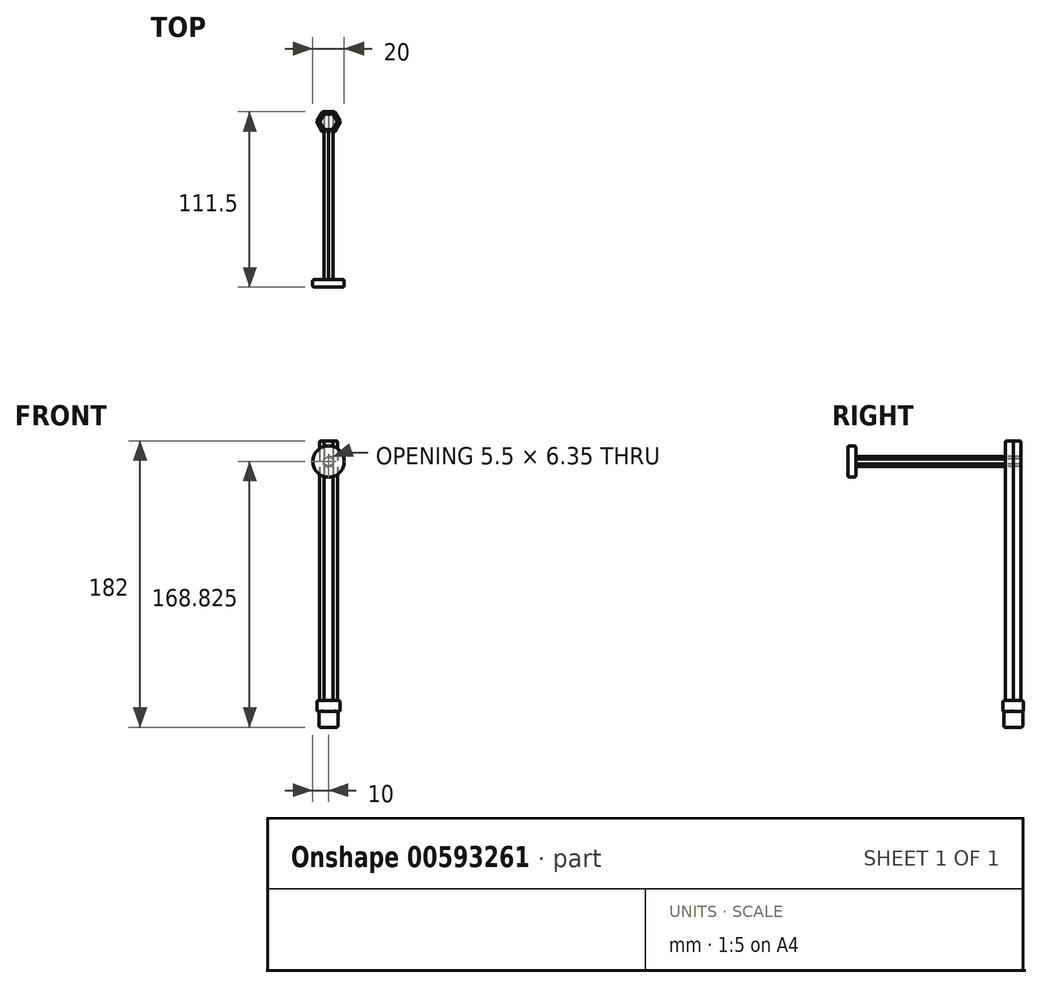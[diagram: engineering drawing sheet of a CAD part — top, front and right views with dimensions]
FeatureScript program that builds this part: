
annotation { "Feature Type Name" : "Feature", "Feature Type Description" : "" }
export const myFeature = defineFeature(function(context is Context, id is Id, definition is map)
    precondition{}
    {
        {
            var Q0;
            Q0=qCreatedBy(makeId("Top.planeOp"),FACE);
            var sketch = newSketch(context, id + "F0", { "sketchPlane" : qUnion([Q0])});
            skCircle(sketch, "E0", {"center": v(0, 0) * mm, "radius": 6 * mm});
            skSolve(sketch);
        }
        {
            var Q0;
            Q0=makeQuery(id+"F0.imprint","IMPRINT",FACE,{"disambiguationData":[TD([[makeQuery(id+"F0.imprint","IMPRINT",EDGE,{"derivedFrom":sQuery(id+"F0.wireOp",EDGE,"E0")}),1.0]])]});
            extrude(context, id + "F1", {"entities" : qUnion([Q0]), "depth" : 17 * mm, "offsetDistance" : 25 * mm});
        }
        {
            var Q0;
            Q0=makeQuery(id+"F1.opExtrude","CAP_FACE",FACE,{"disambiguationData":[OSD([sQuery(id+"F0.wireOp",EDGE,"E0")])],"isStart":false});
            var sketch = newSketch(context, id + "F2", { "sketchPlane" : qUnion([Q0])});
            skCircle(sketch, "E1.cCircle", {"center": v(0, 0) * mm, "radius": 5.47 * mm, "construction": true});
            skCircle(sketch, "E2.cCircle", {"center": v(0, 0) * mm, "radius": 6.5 * mm, "construction": true});
            skLineSegment(sketch, "E2.0", {"start": v(3.75, 6.5) * mm, "end": v(7.5, 0) * mm});
            skLineSegment(sketch, "E2.1", {"start": v(7.5, 0) * mm, "end": v(3.75, -6.5) * mm});
            skLineSegment(sketch, "E2.2", {"start": v(3.75, -6.5) * mm, "end": v(-3.75, -6.5) * mm});
            skLineSegment(sketch, "E2.3", {"start": v(-3.75, -6.5) * mm, "end": v(-7.5, 0) * mm});
            skLineSegment(sketch, "E2.4", {"start": v(-7.5, 0) * mm, "end": v(-3.75, 6.5) * mm});
            skLineSegment(sketch, "E2.5", {"start": v(-3.75, 6.5) * mm, "end": v(3.75, 6.5) * mm});
            skPoint(sketch, "E2.0.midPoint", {"position": v(5.63, 3.25) * mm});
            skSolve(sketch);
        }
        {
            var Q0;
            Q0=makeQuery(id+"F2.imprint","IMPRINT",FACE,{"disambiguationData":[TD([[makeQuery(id+"F2.imprint","IMPRINT",EDGE,{"derivedFrom":sQuery(id+"F2.wireOp",EDGE,"E2.0")}),-1.0]])]});
            extrude(context, id + "F3", {"entities" : qUnion([Q0]), "operationType" : NewBodyOperationType.ADD, "oppositeDirection" : true, "depth" : 7 * mm, "offsetDistance" : 25 * mm});
        }
        {
            var Q0;
            {var subQ0=sQuery(id+"F0.wireOp",EDGE,"E0");Q0=makeQuery(id+"F3.boolean.opBoolean","MERGE",FACE,{"derivedFrom":[makeQuery(id+"F1.opExtrude","CAP_FACE",FACE,{"disambiguationData":[OSD([subQ0])],"isStart":false}),makeQuery(id+"F3.opExtrude","CAP_FACE",FACE,{"disambiguationData":[OSD([subQ0,sQuery(id+"F2.wireOp",EDGE,"E2.0"),sQuery(id+"F2.wireOp",EDGE,"E2.1"),sQuery(id+"F2.wireOp",EDGE,"E2.2"),sQuery(id+"F2.wireOp",EDGE,"E2.3"),sQuery(id+"F2.wireOp",EDGE,"E2.4"),sQuery(id+"F2.wireOp",EDGE,"E2.5")])],"isStart":true})]});}
            var sketch = newSketch(context, id + "F4", { "sketchPlane" : qUnion([Q0])});
            skCircle(sketch, "E3.cCircle", {"center": v(0, 0) * mm, "radius": 5 * mm, "construction": true});
            skLineSegment(sketch, "E3.0", {"start": v(5.77, 0) * mm, "end": v(2.89, -5) * mm});
            skLineSegment(sketch, "E3.1", {"start": v(2.89, -5) * mm, "end": v(-2.89, -5) * mm});
            skLineSegment(sketch, "E3.2", {"start": v(-2.89, -5) * mm, "end": v(-5.77, 0) * mm});
            skLineSegment(sketch, "E3.3", {"start": v(-5.77, 0) * mm, "end": v(-2.89, 5) * mm});
            skLineSegment(sketch, "E3.4", {"start": v(-2.89, 5) * mm, "end": v(2.89, 5) * mm});
            skLineSegment(sketch, "E3.5", {"start": v(2.89, 5) * mm, "end": v(5.77, 0) * mm});
            skPoint(sketch, "E3.0.midPoint", {"position": v(4.33, -2.5) * mm});
            skSolve(sketch);
        }
        {
            var Q0;
            Q0=makeQuery(id+"F4.imprint","IMPRINT",FACE,{"disambiguationData":[TD([[makeQuery(id+"F4.imprint","IMPRINT",EDGE,{"derivedFrom":sQuery(id+"F4.wireOp",EDGE,"E3.0")}),-1.0]])]});
            extrude(context, id + "F5", {"entities" : qUnion([Q0]), "operationType" : NewBodyOperationType.REMOVE, "oppositeDirection" : true, "depth" : 15 * mm, "offsetDistance" : 25 * mm});
        }
        {
            var Q0;
            Q0=makeQuery(id+"F3.opExtrude","SWEPT_FACE",FACE,{"disambiguationData":[OSD([sQuery(id+"F2.wireOp",EDGE,"E2.0")])]});
            var Q1;
            Q1=makeQuery(id+"F3.opExtrude","SWEPT_FACE",FACE,{"disambiguationData":[OSD([sQuery(id+"F2.wireOp",EDGE,"E2.5")])]});
            var Q2;
            Q2=makeQuery(id+"F3.opExtrude","SWEPT_FACE",FACE,{"disambiguationData":[OSD([sQuery(id+"F2.wireOp",EDGE,"E2.4")])]});
            var Q3;
            Q3=makeQuery(id+"F3.opExtrude","SWEPT_FACE",FACE,{"disambiguationData":[OSD([sQuery(id+"F2.wireOp",EDGE,"E2.3")])]});
            var Q4;
            Q4=makeQuery(id+"F3.opExtrude","SWEPT_FACE",FACE,{"disambiguationData":[OSD([sQuery(id+"F2.wireOp",EDGE,"E2.2")])]});
            var Q5;
            Q5=makeQuery(id+"F3.opExtrude","SWEPT_FACE",FACE,{"disambiguationData":[OSD([sQuery(id+"F2.wireOp",EDGE,"E2.1")])]});
            var Q6;
            Q6=makeQuery(id+"F1.opExtrude","CAP_EDGE",EDGE,{"disambiguationData":[OSD([sQuery(id+"F0.wireOp",EDGE,"E0")])],"isStart":true});
            fillet(context, id + "F6", {"entities" : qUnion([Q0, Q1, Q2, Q3, Q4, Q5, Q6]), "radius" : 1 * mm, "tangentPropagation" : true, "allowEdgeOverflow" : false});
        }
        {
            var Q0;
            Q0=makeQuery(id+"F5.boolean.opBoolean","COPY",FACE,{"derivedFrom":makeQuery(id+"F5.opExtrude","CAP_FACE",FACE,{"disambiguationData":[OSD([sQuery(id+"F4.wireOp",EDGE,"E3.0"),sQuery(id+"F4.wireOp",EDGE,"E3.1"),sQuery(id+"F4.wireOp",EDGE,"E3.2"),sQuery(id+"F4.wireOp",EDGE,"E3.3"),sQuery(id+"F4.wireOp",EDGE,"E3.4"),sQuery(id+"F4.wireOp",EDGE,"E3.5")])],"isStart":false})});
            extrude(context, id + "F7", {"entities" : qUnion([Q0]), "operationType" : NewBodyOperationType.ADD, "depth" : 180 * mm, "offsetDistance" : 25 * mm});
        }
        {
            var Q0;
            Q0=makeQuery(id+"F7.opExtrude","SWEPT_FACE",FACE,{"disambiguationData":[OSD([sQuery(id+"F4.wireOp",EDGE,"E3.1")])]});
            var sketch = newSketch(context, id + "F8", { "sketchPlane" : qUnion([Q0])});
            skCircle(sketch, "E4.cCircle", {"center": v(0, 168.82) * mm, "radius": 2.75 * mm, "construction": true});
            skPoint(sketch, "E4.cCircle.centerSnap0", {"position": v(0, 182) * mm});
            skLineSegment(sketch, "E4.0", {"start": v(0, 172) * mm, "end": v(2.75, 170.41) * mm});
            skLineSegment(sketch, "E4.1", {"start": v(2.75, 170.41) * mm, "end": v(2.75, 167.24) * mm});
            skLineSegment(sketch, "E4.2", {"start": v(2.75, 167.24) * mm, "end": v(0, 165.65) * mm});
            skLineSegment(sketch, "E4.3", {"start": v(0, 165.65) * mm, "end": v(-2.75, 167.24) * mm});
            skLineSegment(sketch, "E4.4", {"start": v(-2.75, 167.24) * mm, "end": v(-2.75, 170.41) * mm});
            skLineSegment(sketch, "E4.5", {"start": v(-2.75, 170.41) * mm, "end": v(0, 172) * mm});
            skPoint(sketch, "E4.0.midPoint", {"position": v(1.38, 171.2) * mm});
            skSolve(sketch);
        }
        {
            var Q0;
            Q0=makeQuery(id+"F8.imprint","IMPRINT",FACE,{"disambiguationData":[TD([[makeQuery(id+"F8.imprint","IMPRINT",EDGE,{"derivedFrom":sQuery(id+"F8.wireOp",EDGE,"E4.0")}),-1.0]])]});
            extrude(context, id + "F9", {"entities" : qUnion([Q0]), "operationType" : NewBodyOperationType.REMOVE, "endBound" : BoundingType.THROUGH_ALL, "oppositeDirection" : true, "depth" : 25 * mm, "offsetDistance" : 25 * mm});
        }
        {
            var Q0;
            Q0=makeQuery(id+"F8.imprint","IMPRINT",FACE,{"disambiguationData":[TD([[makeQuery(id+"F8.imprint","IMPRINT",EDGE,{"derivedFrom":sQuery(id+"F8.wireOp",EDGE,"E4.0")}),-1.0]])]});
            extrude(context, id + "F10", {"entities" : qUnion([Q0]), "depth" : 100 * mm, "offsetDistance" : 25 * mm});
        }
        {
            var Q0;
            Q0=makeQuery(id+"F10.opExtrude","CAP_FACE",FACE,{"disambiguationData":[OSD([sQuery(id+"F8.wireOp",EDGE,"E4.0"),sQuery(id+"F8.wireOp",EDGE,"E4.1"),sQuery(id+"F8.wireOp",EDGE,"E4.2"),sQuery(id+"F8.wireOp",EDGE,"E4.3"),sQuery(id+"F8.wireOp",EDGE,"E4.4"),sQuery(id+"F8.wireOp",EDGE,"E4.5")])],"isStart":false});
            fillet(context, id + "F11", {"entities" : qUnion([Q0]), "radius" : 1 * mm, "tangentPropagation" : true, "allowEdgeOverflow" : false});
        }
        {
            var Q0;
            Q0=makeQuery(id+"F9.boolean.opBoolean","INTERSECT",EDGE,{"derivedFrom":[makeQuery(id+"F7.opExtrude","SWEPT_FACE",FACE,{"disambiguationData":[OSD([sQuery(id+"F4.wireOp",EDGE,"E3.4")])]}),makeQuery(id+"F9.opExtrude","SWEPT_FACE",FACE,{"disambiguationData":[OSD([sQuery(id+"F8.wireOp",EDGE,"E4.5")])]})]});
            var Q1;
            Q1=makeQuery(id+"F9.boolean.opBoolean","INTERSECT",EDGE,{"derivedFrom":[makeQuery(id+"F7.opExtrude","SWEPT_FACE",FACE,{"disambiguationData":[OSD([sQuery(id+"F4.wireOp",EDGE,"E3.4")])]}),makeQuery(id+"F9.opExtrude","SWEPT_FACE",FACE,{"disambiguationData":[OSD([sQuery(id+"F8.wireOp",EDGE,"E4.0")])]})]});
            var Q2;
            Q2=makeQuery(id+"F9.boolean.opBoolean","INTERSECT",EDGE,{"derivedFrom":[makeQuery(id+"F7.opExtrude","SWEPT_FACE",FACE,{"disambiguationData":[OSD([sQuery(id+"F4.wireOp",EDGE,"E3.4")])]}),makeQuery(id+"F9.opExtrude","SWEPT_FACE",FACE,{"disambiguationData":[OSD([sQuery(id+"F8.wireOp",EDGE,"E4.1")])]})]});
            var Q3;
            Q3=makeQuery(id+"F9.boolean.opBoolean","INTERSECT",EDGE,{"derivedFrom":[makeQuery(id+"F7.opExtrude","SWEPT_FACE",FACE,{"disambiguationData":[OSD([sQuery(id+"F4.wireOp",EDGE,"E3.4")])]}),makeQuery(id+"F9.opExtrude","SWEPT_FACE",FACE,{"disambiguationData":[OSD([sQuery(id+"F8.wireOp",EDGE,"E4.2")])]})]});
            var Q4;
            Q4=makeQuery(id+"F9.boolean.opBoolean","INTERSECT",EDGE,{"derivedFrom":[makeQuery(id+"F7.opExtrude","SWEPT_FACE",FACE,{"disambiguationData":[OSD([sQuery(id+"F4.wireOp",EDGE,"E3.4")])]}),makeQuery(id+"F9.opExtrude","SWEPT_FACE",FACE,{"disambiguationData":[OSD([sQuery(id+"F8.wireOp",EDGE,"E4.3")])]})]});
            var Q5;
            Q5=makeQuery(id+"F9.boolean.opBoolean","INTERSECT",EDGE,{"derivedFrom":[makeQuery(id+"F7.opExtrude","SWEPT_FACE",FACE,{"disambiguationData":[OSD([sQuery(id+"F4.wireOp",EDGE,"E3.4")])]}),makeQuery(id+"F9.opExtrude","SWEPT_FACE",FACE,{"disambiguationData":[OSD([sQuery(id+"F8.wireOp",EDGE,"E4.4")])]})]});
            var Q6;
            Q6=makeQuery(id+"F9.boolean.opBoolean","COPY",EDGE,{"derivedFrom":makeQuery(id+"F9.opExtrude","CAP_EDGE",EDGE,{"disambiguationData":[OSD([sQuery(id+"F8.wireOp",EDGE,"E4.0")])],"isStart":true})});
            var Q7;
            Q7=makeQuery(id+"F9.boolean.opBoolean","COPY",EDGE,{"derivedFrom":makeQuery(id+"F9.opExtrude","CAP_EDGE",EDGE,{"disambiguationData":[OSD([sQuery(id+"F8.wireOp",EDGE,"E4.5")])],"isStart":true})});
            var Q8;
            Q8=makeQuery(id+"F9.boolean.opBoolean","COPY",EDGE,{"derivedFrom":makeQuery(id+"F9.opExtrude","CAP_EDGE",EDGE,{"disambiguationData":[OSD([sQuery(id+"F8.wireOp",EDGE,"E4.3")])],"isStart":true})});
            var Q9;
            Q9=makeQuery(id+"F9.boolean.opBoolean","COPY",EDGE,{"derivedFrom":makeQuery(id+"F9.opExtrude","CAP_EDGE",EDGE,{"disambiguationData":[OSD([sQuery(id+"F8.wireOp",EDGE,"E4.2")])],"isStart":true})});
            var Q10;
            Q10=makeQuery(id+"F9.boolean.opBoolean","COPY",EDGE,{"derivedFrom":makeQuery(id+"F9.opExtrude","CAP_EDGE",EDGE,{"disambiguationData":[OSD([sQuery(id+"F8.wireOp",EDGE,"E4.1")])],"isStart":true})});
            var Q11;
            Q11=makeQuery(id+"F9.boolean.opBoolean","COPY",EDGE,{"derivedFrom":makeQuery(id+"F9.opExtrude","CAP_EDGE",EDGE,{"disambiguationData":[OSD([sQuery(id+"F8.wireOp",EDGE,"E4.4")])],"isStart":true})});
            fillet(context, id + "F12", {"entities" : qUnion([Q0, Q1, Q2, Q3, Q4, Q5, Q6, Q7, Q8, Q9, Q10, Q11]), "radius" : 1 * mm, "tangentPropagation" : true, "allowEdgeOverflow" : false});
        }
        {
            var Q0;
            Q0=makeQuery(id+"F7.opExtrude","CAP_FACE",FACE,{"disambiguationData":[OSD([sQuery(id+"F4.wireOp",EDGE,"E3.0"),sQuery(id+"F4.wireOp",EDGE,"E3.1"),sQuery(id+"F4.wireOp",EDGE,"E3.2"),sQuery(id+"F4.wireOp",EDGE,"E3.3"),sQuery(id+"F4.wireOp",EDGE,"E3.4"),sQuery(id+"F4.wireOp",EDGE,"E3.5")])],"isStart":false});
            fillet(context, id + "F13", {"entities" : qUnion([Q0]), "radius" : 1 * mm, "tangentPropagation" : true, "allowEdgeOverflow" : false});
        }
        {
            var Q0;
            Q0=makeQuery(id+"F10.opExtrude","CAP_FACE",FACE,{"disambiguationData":[OSD([sQuery(id+"F8.wireOp",EDGE,"E4.0"),sQuery(id+"F8.wireOp",EDGE,"E4.1"),sQuery(id+"F8.wireOp",EDGE,"E4.2"),sQuery(id+"F8.wireOp",EDGE,"E4.3"),sQuery(id+"F8.wireOp",EDGE,"E4.4"),sQuery(id+"F8.wireOp",EDGE,"E4.5")])],"isStart":false});
            var sketch = newSketch(context, id + "F14", { "sketchPlane" : qUnion([Q0])});
            skLineSegment(sketch, "E5.0", {"start": v(0, 170.85) * mm, "end": v(-1.75, 169.83) * mm});
            skLineSegment(sketch, "E6.0", {"start": v(1.75, 169.83) * mm, "end": v(0, 170.85) * mm});
            skLineSegment(sketch, "E7.0", {"start": v(1.75, 167.81) * mm, "end": v(1.75, 169.83) * mm});
            skLineSegment(sketch, "E8.0", {"start": v(0, 166.8) * mm, "end": v(1.75, 167.81) * mm});
            skLineSegment(sketch, "E9.0", {"start": v(-1.75, 167.81) * mm, "end": v(0, 166.8) * mm});
            skLineSegment(sketch, "E10.0", {"start": v(-1.75, 169.83) * mm, "end": v(-1.75, 167.81) * mm});
            skLineSegment(sketch, "E11", {"start": v(1.75, 167.81) * mm, "end": v(-1.75, 169.83) * mm});
            skLineSegment(sketch, "E12", {"start": v(0, 170.85) * mm, "end": v(0, 166.8) * mm});
            skLineSegment(sketch, "E13", {"start": v(-1.75, 167.81) * mm, "end": v(1.75, 169.83) * mm});
            skCircle(sketch, "E14", {"center": v(0, 168.82) * mm, "radius": 10 * mm});
            skSolve(sketch);
        }
        {
            var Q0;
            Q0=makeQuery(id+"F14.imprint","IMPRINT",FACE,{"disambiguationData":[TD([[makeQuery(id+"F14.imprint","IMPRINT",EDGE,{"derivedFrom":sQuery(id+"F14.wireOp",EDGE,"E5.0")}),-1.0]])]});
            var Q1;
            {var subQ0=sQuery(id+"F14.wireOp",EDGE,"E6.0");Q1=makeQuery(id+"F14.imprint","IMPRINT",FACE,{"disambiguationData":[TD([[makeQuery(id+"F14.imprint","IMPRINT",EDGE,{"derivedFrom":subQ0}),1.0]])]});}
            var Q2;
            {var subQ0=sQuery(id+"F14.wireOp",EDGE,"E5.0");Q2=makeQuery(id+"F14.imprint","IMPRINT",FACE,{"disambiguationData":[TD([[makeQuery(id+"F14.imprint","IMPRINT",EDGE,{"derivedFrom":subQ0}),1.0]])]});}
            var Q3;
            {var subQ0=sQuery(id+"F14.wireOp",EDGE,"E10.0");Q3=makeQuery(id+"F14.imprint","IMPRINT",FACE,{"disambiguationData":[TD([[makeQuery(id+"F14.imprint","IMPRINT",EDGE,{"derivedFrom":subQ0}),1.0]])]});}
            var Q4;
            {var subQ0=sQuery(id+"F14.wireOp",EDGE,"E9.0");Q4=makeQuery(id+"F14.imprint","IMPRINT",FACE,{"disambiguationData":[TD([[makeQuery(id+"F14.imprint","IMPRINT",EDGE,{"derivedFrom":subQ0}),1.0]])]});}
            var Q5;
            {var subQ0=sQuery(id+"F14.wireOp",EDGE,"E8.0");Q5=makeQuery(id+"F14.imprint","IMPRINT",FACE,{"disambiguationData":[TD([[makeQuery(id+"F14.imprint","IMPRINT",EDGE,{"derivedFrom":subQ0}),1.0]])]});}
            var Q6;
            {var subQ0=sQuery(id+"F14.wireOp",EDGE,"E7.0");Q6=makeQuery(id+"F14.imprint","IMPRINT",FACE,{"disambiguationData":[TD([[makeQuery(id+"F14.imprint","IMPRINT",EDGE,{"derivedFrom":subQ0}),1.0]])]});}
            extrude(context, id + "F15", {"entities" : qUnion([Q0, Q1, Q2, Q3, Q4, Q5, Q6]), "operationType" : NewBodyOperationType.ADD, "oppositeDirection" : true, "depth" : 5 * mm, "offsetDistance" : 25 * mm});
        }
        {
            var Q0;
            Q0=makeQuery(id+"F15.opExtrude","CAP_EDGE",EDGE,{"disambiguationData":[OSD([sQuery(id+"F14.wireOp",EDGE,"E14")])],"isStart":false});
            var Q1;
            Q1=makeQuery(id+"F15.opExtrude","CAP_EDGE",EDGE,{"disambiguationData":[OSD([sQuery(id+"F14.wireOp",EDGE,"E14")])],"isStart":true});
            fillet(context, id + "F16", {"entities" : qUnion([Q0, Q1]), "radius" : 1 * mm, "tangentPropagation" : true, "allowEdgeOverflow" : false});
        }
    });
